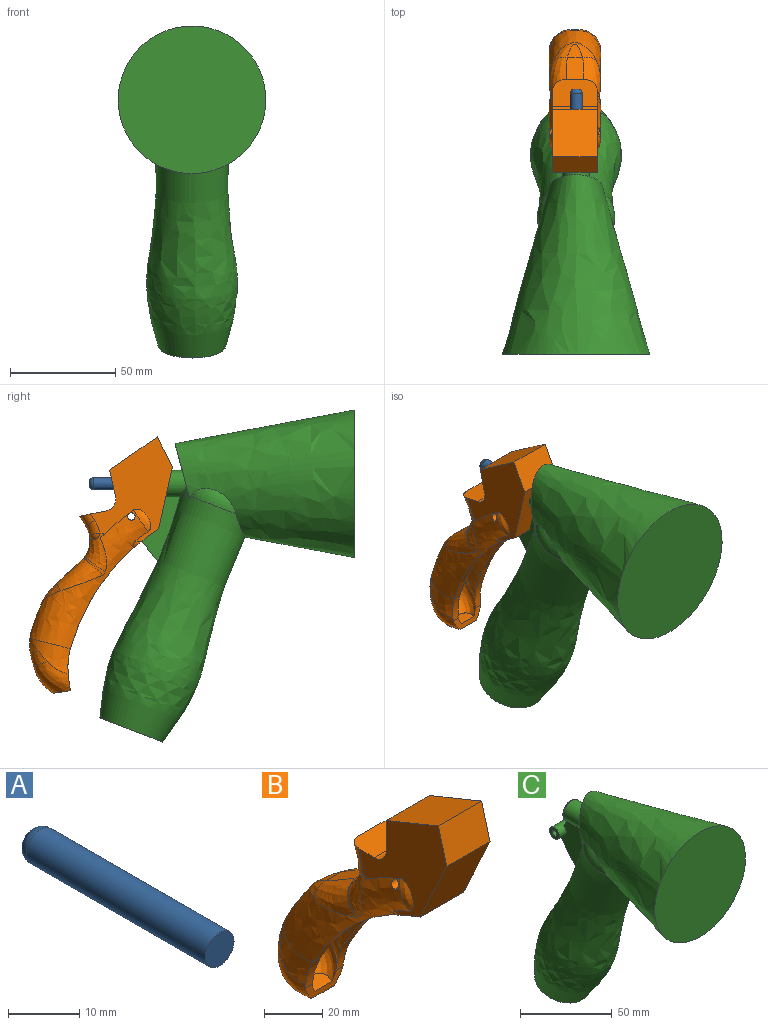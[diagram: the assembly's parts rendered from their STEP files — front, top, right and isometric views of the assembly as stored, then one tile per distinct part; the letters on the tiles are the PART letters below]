
ASSEMBLY  parts=3 mates=2
PART A: 4 faces, bbox 5.7x37.6x5.7 mm
  f0: cylinder r=2.85mm len=35.6mm, axis (0,-1,0), area 637.5mm2, adj f2,f3
  f1: plane 1.7x1.7mm, normal (0,1,0), area 2.3mm2, adj f3
  f2: plane 5.7x5.7mm, normal (0,-1,0), area 25.5mm2, adj f0
  f3: torus R=0.85mm, axis (0,1,0), area 41.9mm2, adj f0,f1
PART B: 86 faces, bbox 44.8x98.3x122.9 mm
  f0: bspline ~71.61x65.58mm, area 2207.4mm2, adj f1,f2,f3,f19,f24,f25,f26,f27
  f1: cylinder r=1.75mm len=21.34mm, axis (-1,0,0), area 234.7mm2, adj f0
  f2: bspline ~15.53x9.97mm, area 0mm2, adj f0,f85
  f3: cylinder r=5mm len=3.08mm, axis (0,-0.91,-0.42), area 2.8mm2, adj f0,f4,f28,f85
  f4: sphere r=5mm, area 14.6mm2, adj f3,f5,f18,f28
  f5: torus R=18.36mm, axis (1,0,0), area 41.4mm2, adj f4,f6,f17,f85
  f6: cylinder r=13.36mm len=11mm, axis (-1,0,0), area 51mm2, adj f5,f7,f16,f18
  f7: torus R=18.36mm, axis (1,0,0), area 41.4mm2, adj f6,f8,f15,f31
  f8: cylinder r=5mm len=6.72mm, axis (0,0.32,0.95), area 35.6mm2, adj f7,f9,f16,f31
  f9: plane 21.75x13.47mm, normal (0,-0.02,1), area 255.8mm2, adj f8,f10,f16,f17,f31,f85
  f10: cylinder r=5.71mm len=21mm, axis (-1,0,0), area 190.8mm2, adj f9,f11,f31,f85
  f11: plane 21x12.8mm, normal (0,1,0), area 268.8mm2, adj f10,f12,f31,f85
  f12: plane 25.4x21mm, normal (0,0.38,0.93), area 576.3mm2, adj f11,f13,f31,f85
  f13: plane 21x15.09mm, normal (0,-0.97,0.26), area 328.1mm2, adj f12,f14,f31,f85
  f14: plane 27.65x21mm, normal (0,-0.91,-0.42), area 640.6mm2, adj f13,f31,f66,f85
  f15: sphere r=5mm, area 14.6mm2, adj f7,f18,f28,f29
  f16: plane 11x5.14mm, normal (0,0.95,-0.32), area 59.6mm2, adj f6,f8,f9,f17
  f17: cylinder r=5mm len=6.72mm, axis (0,-0.32,-0.95), area 35.6mm2, adj f5,f9,f16,f85
  f18: cylinder r=5mm len=11mm, axis (-1,0,0), area 13.4mm2, adj f4,f6,f15,f28
  f19: bspline ~14.08x13.15mm, area 14.6mm2, adj f0,f20,f22,f24,f28
  f20: plane 7.31x0.58mm, normal (0,0.67,0.75), area 5.6mm2, adj f19,f21,f22,f27
  f21: cylinder r=13.36mm len=8.38mm, axis (-1,0,0), area 67mm2, adj f20,f28
  f22: plane 14.69x8.51mm, normal (0,0.5,0.87), area 135.7mm2, adj f19,f20,f23,f24,f26,f27
  f23: cylinder r=40.91mm len=7.86mm, axis (-1,0,0), area 45.5mm2, adj f22,f25
  f24: bspline ~25.8x15.1mm, area 239.7mm2, adj f0,f19,f22,f25
  f25: bspline ~21.3x10.99mm, area 116.2mm2, adj f0,f23,f24,f26
  f26: bspline ~25.8x15.1mm, area 239.7mm2, adj f0,f22,f25,f27
  f27: bspline ~14.08x13.15mm, area 14.6mm2, adj f0,f20,f22,f26,f28
  f28: bspline ~34.74x23.59mm, area 310.9mm2, adj f0,f3,f4,f15,f18,f19,f21,f27
  f29: cylinder r=5mm len=3.08mm, axis (0,0.91,0.42), area 2.8mm2, adj f0,f15,f28,f31
  f30: bspline ~15.55x9.98mm, area 0mm2, adj f0,f31
  f31: plane 55.08x50.92mm, normal (-1,0,0), area 912.2mm2, adj f0,f7,f8,f9,f10,f11,f12,f13
  f32: cylinder r=5mm len=4.11mm, axis (0,0.91,0.42), area 4.1mm2, adj f0,f31,f66
  f33: bspline ~24.87x22.16mm, area 167.6mm2, adj f0,f34,f59,f60,f61,f62
  f34: bspline ~8.25x8.11mm, area 44.1mm2, adj f33,f35,f61,f62
  f35: cylinder r=22.54mm len=9.56mm, axis (-1,0,0), area 43.7mm2, adj f34,f36,f57,f58,f62,f64
  f36: bspline ~10.41x9.35mm, area 44.1mm2, adj f35,f37,f64,f65
  f37: bspline ~9.47x9.01mm, area 58.6mm2, adj f36,f38,f58,f65
  f38: bspline ~24.2x18.98mm, area 252.9mm2, adj f37,f39,f54,f55,f56,f65
  f39: plane 18.44x6.84mm, normal (0,-1,-0.09), area 58.4mm2, adj f38,f40,f52,f53,f54,f56,f59,f60
  f40: bspline ~20.28x14.63mm, area 153.5mm2, adj f39,f41,f51,f52,f59
  f41: cylinder r=19.25mm len=12.13mm, axis (-1,0,0), area 72.7mm2, adj f40,f42,f52,f53
  f42: plane 8.29x4.87mm, normal (0,-1,0.04), area 37.9mm2, adj f41,f43,f50,f51
  f43: bspline ~10.2x6.75mm, area 38.2mm2, adj f42,f44,f53
  f44: bspline ~9.02x7.09mm, area 27mm2, adj f43,f45,f50
  f45: bspline ~4.12x4.1mm, area 5.4mm2, adj f44,f46,f50
  f46: bspline ~5.19x1.86mm, area 3.1mm2, adj f45,f47,f49
  f47: bspline ~4.12x4.1mm, area 5.4mm2, adj f46,f48,f50
  f48: bspline ~9.02x7.09mm, area 27mm2, adj f47,f50,f51
  f49: plane 1.75x0.76mm, normal (0,-0.92,-0.39), area 1mm2, adj f46,f50
  f50: cylinder r=20.04mm len=8.5mm, axis (-1,0,0), area 38.8mm2, adj f42,f44,f45,f47,f48,f49
  f51: bspline ~10.2x6.75mm, area 38.2mm2, adj f40,f42,f48
  f52: plane 10.24x7.22mm, normal (0,-0.07,1), area 66mm2, adj f39,f40,f41,f53
  f53: bspline ~20.28x14.63mm, area 153.5mm2, adj f39,f41,f43,f52,f54
  f54: cylinder r=33.68mm len=12.88mm, axis (-1,0,0), area 48.4mm2, adj f38,f39,f53,f65,f66
  f55: cylinder r=21.75mm len=14.46mm, axis (-1,0,0), area 108.2mm2, adj f38,f56,f58,f60
  f56: plane 12.08x8.15mm, normal (0,0.07,-1), area 86.9mm2, adj f38,f39,f55,f60
  f57: plane 1.75x0.76mm, normal (0,0.92,0.39), area 1mm2, adj f35,f63
  f58: plane 8.29x4.87mm, normal (0,1,-0.04), area 37.9mm2, adj f35,f37,f55,f61
  f59: cylinder r=33.68mm len=12.88mm, axis (-1,0,0), area 48.4mm2, adj f33,f39,f40,f60,f66
  f60: bspline ~24.2x18.98mm, area 252.9mm2, adj f33,f39,f55,f56,f59,f61
  f61: bspline ~9.47x9.01mm, area 58.6mm2, adj f33,f34,f58,f60
  f62: bspline ~5.34x4.76mm, area 8.7mm2, adj f0,f33,f34,f35,f63
  f63: bspline ~5.85x1.86mm, area 5mm2, adj f0,f57,f62,f64
  f64: bspline ~5.34x4.76mm, area 8.7mm2, adj f0,f35,f36,f63,f65
  f65: bspline ~24.87x22.16mm, area 167.6mm2, adj f0,f36,f37,f38,f54,f64
  f66: cylinder r=98.5mm len=53.31mm, axis (-1,0,0), area 741.9mm2, adj f0,f14,f31,f32,f54,f59,f67,f82
  f67: cylinder r=5mm len=15.52mm, axis (0,0.91,0.42), area 58.2mm2, adj f66,f68,f81,f82
  f68: sphere r=5mm, area 0.7mm2, adj f67,f69,f81
  f69: cylinder r=5mm len=11mm, axis (-1,0,0), area 12.2mm2, adj f68,f70,f71,f80,f81,f82
  f70: sphere r=5mm, area 0.7mm2, adj f69,f71,f83
  f71: bspline ~17.01x9.94mm, area 98.7mm2, adj f69,f70,f72,f80,f83
  f72: bspline ~10.31x9.74mm, area 12.6mm2, adj f71,f73,f78,f79
  f73: plane 7.31x0.77mm, normal (0,-0.67,-0.75), area 7.5mm2, adj f72,f74,f78,f80
  f74: bspline ~10.31x9.74mm, area 12.6mm2, adj f73,f75,f78,f81
  f75: bspline ~23.36x13.37mm, area 162.7mm2, adj f74,f76,f78
  f76: bspline ~17.35x10.03mm, area 73.8mm2, adj f75,f77,f79
  f77: cylinder r=38.41mm len=7.38mm, axis (-1,0,0), area 42.8mm2, adj f76,f78
  f78: plane 14.91x8.64mm, normal (0,-0.5,-0.87), area 137.6mm2, adj f72,f73,f74,f75,f77,f79
  f79: bspline ~23.36x13.37mm, area 162.7mm2, adj f72,f76,f78
  f80: cylinder r=15.86mm len=7.46mm, axis (-1,0,0), area 63.2mm2, adj f69,f71,f73,f81
  f81: bspline ~16.73x9.84mm, area 98.7mm2, adj f67,f68,f69,f74,f80
  f82: plane 14.56x11mm, normal (0,0.42,-0.91), area 176.7mm2, adj f66,f67,f69,f83
  f83: cylinder r=5mm len=15.52mm, axis (0,-0.91,-0.42), area 58.2mm2, adj f66,f70,f71,f82
  f84: cylinder r=5mm len=4.11mm, axis (0,-0.91,-0.42), area 4.1mm2, adj f0,f66,f85
  f85: plane 55.08x50.92mm, normal (1,0,0), area 912.2mm2, adj f0,f2,f3,f5,f9,f10,f11,f12
PART C: 24 faces, bbox 70.1x120.8x157.5 mm
  f0: plane 70x70mm, normal (0,-1,0), area 3848.5mm2, adj f2
  f1: plane 26.14x25.2mm, normal (0,0.97,-0.26), area 352.2mm2, adj f2,f3,f6,f8,f9
  f2: bspline ~85.61x70mm, area 12088.4mm2, adj f0,f1,f6,f7,f12
  f3: cylinder r=6.35mm len=19.34mm, axis (0,-1,0), area 666.5mm2, adj f1,f5,f6,f8,f9,f16,f17
  f4: plane 10.7x10.55mm, normal (0,1,0), area 63.8mm2, adj f5,f10,f16,f17,f22
  f5: torus R=5.35mm, axis (0,-1,0), area 55mm2, adj f3,f4,f16,f17
  f6: revolved ~118.16x72.6mm, area 13107.8mm2, adj f1,f2,f3,f7,f8,f9,f11,f12
  f7: torus R=8.05mm, axis (0,-0.36,0.93), area 126.8mm2, adj f2,f6
  f8: torus R=8.05mm, axis (0,-0.36,0.93), area 15.6mm2, adj f1,f3,f6
  f9: torus R=8.05mm, axis (0,-0.36,0.93), area 15.6mm2, adj f1,f3,f6
  f10: plane 7.2x3.95mm, normal (0,0.88,0.48), area 20.5mm2, adj f4,f16,f17,f18
  f11: plane 32x29.87mm, normal (0,0.36,-0.93), area 218.9mm2, adj f6,f13
  f12: torus R=8.05mm, axis (0,-0.36,0.93), area 126.8mm2, adj f2,f6
  f13: cylinder r=13.65mm len=29.07mm, axis (0,0.36,-0.93), area 857.7mm2, adj f11,f14
  f14: plane 27.3x25.49mm, normal (0,0.36,-0.93), area 585.3mm2, adj f13
  f15: plane 18.88x15.57mm, normal (0,0.77,-0.64), area 60.9mm2, adj f6,f16,f17,f18
  f16: plane 31.8x26.12mm, normal (1,0,0), area 422mm2, adj f3,f4,f5,f6,f10,f15,f18
  f17: plane 31.8x26.12mm, normal (-1,0,0), area 422mm2, adj f3,f4,f5,f6,f10,f15,f18
  f18: cylinder r=3.75mm len=13mm, axis (-1,0,0), area 273.4mm2, adj f10,f15,f16,f17,f20,f21
  f19: cylinder r=1.75mm len=13mm, axis (-1,0,0), area 142.9mm2, adj f20,f21
  f20: plane 7.5x7.5mm, normal (1,0,0), area 34.6mm2, adj f18,f19
  f21: plane 7.5x7.5mm, normal (-1,0,0), area 34.6mm2, adj f18,f19
  f22: cylinder r=2.85mm len=20.6mm, axis (0,-1,0), area 368.9mm2, adj f4,f23
  f23: plane 5.7x5.7mm, normal (0,1,0), area 25.5mm2, adj f22
PLACE A rot(axis=(0,-1,0),82.4deg) t=(-48.85,-37.01,3.14)mm
PLACE B rot(axis=(-1,0,0),12.7deg) t=(-49.35,-39.76,25.95)mm
PLACE C t=(-48.85,-45.73,3.14)mm fixed
MATE cylindrical C.f22 <-> A.f0  axis (0,1,0) through (-48.85,54.27,3.14)mm
MATE revolute B.f1 <-> C.f18  axis (-1,0,0) through (-49.35,60.07,-12.36)mm
